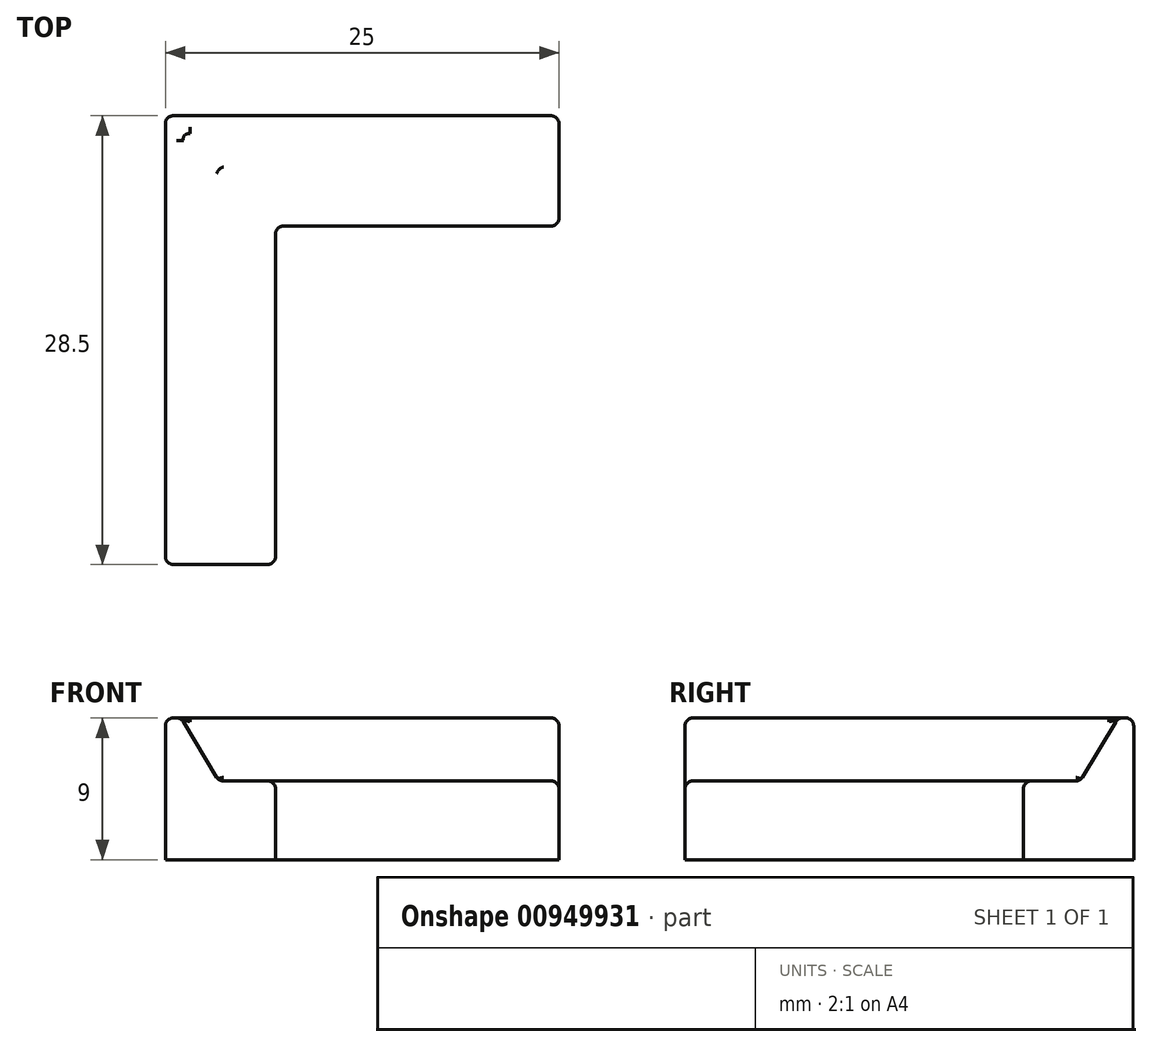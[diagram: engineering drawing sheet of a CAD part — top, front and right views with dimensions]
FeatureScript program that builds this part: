
annotation { "Feature Type Name" : "Feature", "Feature Type Description" : "" }
export const myFeature = defineFeature(function(context is Context, id is Id, definition is map)
    precondition{}
    {
        {
            var Q0;
            Q0=qCreatedBy(makeId("Top.planeOp"),FACE);
            var sketch = newSketch(context, id + "F0", { "sketchPlane" : qUnion([Q0])});
            skLineSegment(sketch, "E0.bottom", {"start": v(-48.09, 20.85) * mm, "end": v(-41.09, 20.85) * mm});
            skLineSegment(sketch, "E0.top", {"start": v(-48.09, -7.65) * mm, "end": v(-41.09, -7.65) * mm});
            skLineSegment(sketch, "E0.left", {"start": v(-48.09, 20.85) * mm, "end": v(-48.09, -7.65) * mm});
            skLineSegment(sketch, "E0.right", {"start": v(-41.09, 20.85) * mm, "end": v(-41.09, -7.65) * mm});
            skLineSegment(sketch, "E1.bottom", {"start": v(-41.09, 20.85) * mm, "end": v(-23.09, 20.85) * mm});
            skLineSegment(sketch, "E1.top", {"start": v(-41.09, 13.85) * mm, "end": v(-23.09, 13.85) * mm});
            skLineSegment(sketch, "E1.left", {"start": v(-41.09, 20.85) * mm, "end": v(-41.09, 13.85) * mm});
            skLineSegment(sketch, "E1.right", {"start": v(-23.09, 20.85) * mm, "end": v(-23.09, 13.85) * mm});
            skSolve(sketch);
        }
        {
            var Q0;
            Q0 = qSketchRegion(id + "F0", true);
            extrude(context, id + "F1", {"entities" : qUnion([Q0]), "depth" : 5 * mm, "offsetDistance" : 25 * mm});
        }
        {
            var Q0;
            Q0=makeQuery(id+"F1.opExtrude","CAP_FACE",FACE,{"disambiguationData":[OSD([sQuery(id+"F0.wireOp",EDGE,"E0.bottom"),sQuery(id+"F0.wireOp",EDGE,"E0.top"),sQuery(id+"F0.wireOp",EDGE,"E0.left"),sQuery(id+"F0.wireOp",EDGE,"E0.right"),sQuery(id+"F0.wireOp",EDGE,"E1.bottom"),sQuery(id+"F0.wireOp",EDGE,"E1.top"),sQuery(id+"F0.wireOp",EDGE,"E1.right")])],"isStart":false});
            var sketch = newSketch(context, id + "F2", { "sketchPlane" : qUnion([Q0])});
            skLineSegment(sketch, "E2.bottom", {"start": v(-48.09, 20.85) * mm, "end": v(-44.09, 20.85) * mm});
            skLineSegment(sketch, "E2.top", {"start": v(-48.09, -7.65) * mm, "end": v(-44.09, -7.65) * mm});
            skLineSegment(sketch, "E2.left", {"start": v(-48.09, 20.85) * mm, "end": v(-48.09, -7.65) * mm});
            skLineSegment(sketch, "E2.right", {"start": v(-44.09, 20.85) * mm, "end": v(-44.09, -7.65) * mm});
            skLineSegment(sketch, "E3.bottom", {"start": v(-44.09, 20.85) * mm, "end": v(-23.09, 20.85) * mm});
            skLineSegment(sketch, "E3.top", {"start": v(-44.09, 16.85) * mm, "end": v(-23.09, 16.85) * mm});
            skLineSegment(sketch, "E3.left", {"start": v(-44.09, 20.85) * mm, "end": v(-44.09, 16.85) * mm});
            skLineSegment(sketch, "E3.right", {"start": v(-23.09, 20.85) * mm, "end": v(-23.09, 16.85) * mm});
            skSolve(sketch);
        }
        {
            var Q0;
            Q0 = qSketchRegion(id + "F2", true);
            extrude(context, id + "F3", {"entities" : qUnion([Q0]), "operationType" : NewBodyOperationType.ADD, "depth" : 4 * mm, "offsetDistance" : 25 * mm});
        }
        {
            var Q0;
            Q0=makeQuery(id+"F3.opExtrude","CAP_EDGE",EDGE,{"disambiguationData":[OSD([sQuery(id+"F2.wireOp",EDGE,"E2.right")])],"isStart":false});
            var Q1;
            Q1=makeQuery(id+"F3.opExtrude","CAP_EDGE",EDGE,{"disambiguationData":[OSD([sQuery(id+"F2.wireOp",EDGE,"E3.top")])],"isStart":false});
            chamfer(context, id + "F4", {"entities" : qUnion([Q0, Q1]), "chamferType" : ChamferType.TWO_OFFSETS, "width1" : 5 * mm, "oppositeDirection" : false, "width2" : 3 * mm, "tangentPropagation" : true});
        }
        {
            var Q0;
            Q0=makeQuery(id+"F3.boolean.opBoolean","MERGE",EDGE,{"derivedFrom":[makeQuery(id+"F1.opExtrude","SWEPT_EDGE",EDGE,{"disambiguationData":[OSD([sQuery(id+"F0.wireOp",EDGE,"E0.top"),sQuery(id+"F0.wireOp",EDGE,"E0.left")])]}),makeQuery(id+"F3.opExtrude","SWEPT_EDGE",EDGE,{"disambiguationData":[OSD([sQuery(id+"F2.wireOp",EDGE,"E2.top"),sQuery(id+"F2.wireOp",EDGE,"E2.left")])]})]});
            var Q1;
            Q1=makeQuery(id+"F1.opExtrude","SWEPT_EDGE",EDGE,{"disambiguationData":[OSD([sQuery(id+"F0.wireOp",EDGE,"E0.top"),sQuery(id+"F0.wireOp",EDGE,"E0.right")])]});
            var Q2;
            Q2=makeQuery(id+"F1.opExtrude","SWEPT_EDGE",EDGE,{"disambiguationData":[OSD([sQuery(id+"F0.wireOp",EDGE,"E0.right"),sQuery(id+"F0.wireOp",EDGE,"E1.top"),sQuery(id+"F0.wireOp",EDGE,"E1.left")])]});
            var Q3;
            Q3=makeQuery(id+"F1.opExtrude","SWEPT_EDGE",EDGE,{"disambiguationData":[OSD([sQuery(id+"F0.wireOp",EDGE,"E1.top"),sQuery(id+"F0.wireOp",EDGE,"E1.right")])]});
            var Q4;
            Q4=makeQuery(id+"F3.boolean.opBoolean","MERGE",EDGE,{"derivedFrom":[makeQuery(id+"F1.opExtrude","SWEPT_EDGE",EDGE,{"disambiguationData":[OSD([sQuery(id+"F0.wireOp",EDGE,"E1.bottom"),sQuery(id+"F0.wireOp",EDGE,"E1.right")])]}),makeQuery(id+"F3.opExtrude","SWEPT_EDGE",EDGE,{"disambiguationData":[OSD([sQuery(id+"F2.wireOp",EDGE,"E3.bottom"),sQuery(id+"F2.wireOp",EDGE,"E3.right")])]})]});
            var Q5;
            Q5=makeQuery(id+"F3.opExtrude","CAP_EDGE",EDGE,{"disambiguationData":[OSD([sQuery(id+"F2.wireOp",EDGE,"E2.bottom"),sQuery(id+"F2.wireOp",EDGE,"E3.bottom")])],"isStart":false});
            var Q6;
            {var subQ0=sQuery(id+"F2.wireOp",EDGE,"E3.top");Q6=makeQuery(id+"F4.opChamfer","BLEND_EDGE",EDGE,{"blendedFrom":[makeQuery(id+"F3.opExtrude","CAP_EDGE",EDGE,{"disambiguationData":[OSD([subQ0])],"isStart":false}),makeQuery(id+"F3.opExtrude","CAP_FACE",FACE,{"disambiguationData":[OSD([sQuery(id+"F2.wireOp",EDGE,"E2.bottom"),sQuery(id+"F2.wireOp",EDGE,"E2.top"),sQuery(id+"F2.wireOp",EDGE,"E2.left"),sQuery(id+"F2.wireOp",EDGE,"E2.right"),sQuery(id+"F2.wireOp",EDGE,"E3.bottom"),subQ0,sQuery(id+"F2.wireOp",EDGE,"E3.right")])],"isStart":false})],"blendedInto":[makeQuery(id+"F3.opExtrude","CAP_FACE",FACE,{"disambiguationData":[OSD([sQuery(id+"F2.wireOp",EDGE,"E2.bottom"),sQuery(id+"F2.wireOp",EDGE,"E2.top"),sQuery(id+"F2.wireOp",EDGE,"E2.left"),sQuery(id+"F2.wireOp",EDGE,"E2.right"),sQuery(id+"F2.wireOp",EDGE,"E3.bottom"),subQ0,sQuery(id+"F2.wireOp",EDGE,"E3.right")])],"isStart":false})]});}
            var Q7;
            {var subQ0=sQuery(id+"F2.wireOp",EDGE,"E2.right");Q7=makeQuery(id+"F4.opChamfer","BLEND_EDGE",EDGE,{"blendedFrom":[makeQuery(id+"F3.opExtrude","CAP_EDGE",EDGE,{"disambiguationData":[OSD([subQ0])],"isStart":false}),makeQuery(id+"F3.opExtrude","CAP_FACE",FACE,{"disambiguationData":[OSD([sQuery(id+"F2.wireOp",EDGE,"E2.bottom"),sQuery(id+"F2.wireOp",EDGE,"E2.top"),sQuery(id+"F2.wireOp",EDGE,"E2.left"),subQ0,sQuery(id+"F2.wireOp",EDGE,"E3.bottom"),sQuery(id+"F2.wireOp",EDGE,"E3.top"),sQuery(id+"F2.wireOp",EDGE,"E3.right")])],"isStart":false})],"blendedInto":[makeQuery(id+"F3.opExtrude","CAP_FACE",FACE,{"disambiguationData":[OSD([sQuery(id+"F2.wireOp",EDGE,"E2.bottom"),sQuery(id+"F2.wireOp",EDGE,"E2.top"),sQuery(id+"F2.wireOp",EDGE,"E2.left"),subQ0,sQuery(id+"F2.wireOp",EDGE,"E3.bottom"),sQuery(id+"F2.wireOp",EDGE,"E3.top"),sQuery(id+"F2.wireOp",EDGE,"E3.right")])],"isStart":false})]});}
            var Q8;
            Q8=makeQuery(id+"F4.opChamfer","BLEND_EDGE",EDGE,{"blendedFrom":[makeQuery(id+"F3.opExtrude","CAP_EDGE",EDGE,{"disambiguationData":[OSD([sQuery(id+"F2.wireOp",EDGE,"E2.right")])],"isStart":false}),makeQuery(id+"F3.opExtrude","CAP_EDGE",EDGE,{"disambiguationData":[OSD([sQuery(id+"F2.wireOp",EDGE,"E3.top")])],"isStart":false})],"blendedInto":[]});
            var Q9;
            Q9=makeQuery(id+"F4.opChamfer","BLEND_EDGE",EDGE,{"blendedFrom":[makeQuery(id+"F3.opExtrude","CAP_EDGE",EDGE,{"disambiguationData":[OSD([sQuery(id+"F2.wireOp",EDGE,"E3.top")])],"isStart":false}),makeQuery(id+"F1.opExtrude","CAP_FACE",FACE,{"disambiguationData":[OSD([sQuery(id+"F0.wireOp",EDGE,"E0.bottom"),sQuery(id+"F0.wireOp",EDGE,"E0.top"),sQuery(id+"F0.wireOp",EDGE,"E0.left"),sQuery(id+"F0.wireOp",EDGE,"E0.right"),sQuery(id+"F0.wireOp",EDGE,"E1.bottom"),sQuery(id+"F0.wireOp",EDGE,"E1.top"),sQuery(id+"F0.wireOp",EDGE,"E1.right")])],"isStart":false})],"blendedInto":[makeQuery(id+"F1.opExtrude","CAP_FACE",FACE,{"disambiguationData":[OSD([sQuery(id+"F0.wireOp",EDGE,"E0.bottom"),sQuery(id+"F0.wireOp",EDGE,"E0.top"),sQuery(id+"F0.wireOp",EDGE,"E0.left"),sQuery(id+"F0.wireOp",EDGE,"E0.right"),sQuery(id+"F0.wireOp",EDGE,"E1.bottom"),sQuery(id+"F0.wireOp",EDGE,"E1.top"),sQuery(id+"F0.wireOp",EDGE,"E1.right")])],"isStart":false})]});
            var Q10;
            Q10=makeQuery(id+"F4.opChamfer","BLEND_EDGE",EDGE,{"blendedFrom":[makeQuery(id+"F3.opExtrude","CAP_EDGE",EDGE,{"disambiguationData":[OSD([sQuery(id+"F2.wireOp",EDGE,"E2.right")])],"isStart":false}),makeQuery(id+"F1.opExtrude","CAP_FACE",FACE,{"disambiguationData":[OSD([sQuery(id+"F0.wireOp",EDGE,"E0.bottom"),sQuery(id+"F0.wireOp",EDGE,"E0.top"),sQuery(id+"F0.wireOp",EDGE,"E0.left"),sQuery(id+"F0.wireOp",EDGE,"E0.right"),sQuery(id+"F0.wireOp",EDGE,"E1.bottom"),sQuery(id+"F0.wireOp",EDGE,"E1.top"),sQuery(id+"F0.wireOp",EDGE,"E1.right")])],"isStart":false})],"blendedInto":[makeQuery(id+"F1.opExtrude","CAP_FACE",FACE,{"disambiguationData":[OSD([sQuery(id+"F0.wireOp",EDGE,"E0.bottom"),sQuery(id+"F0.wireOp",EDGE,"E0.top"),sQuery(id+"F0.wireOp",EDGE,"E0.left"),sQuery(id+"F0.wireOp",EDGE,"E0.right"),sQuery(id+"F0.wireOp",EDGE,"E1.bottom"),sQuery(id+"F0.wireOp",EDGE,"E1.top"),sQuery(id+"F0.wireOp",EDGE,"E1.right")])],"isStart":false})]});
            var Q11;
            Q11=makeQuery(id+"F1.opExtrude","CAP_EDGE",EDGE,{"disambiguationData":[OSD([sQuery(id+"F0.wireOp",EDGE,"E0.right")])],"isStart":false});
            var Q12;
            Q12=makeQuery(id+"F1.opExtrude","CAP_EDGE",EDGE,{"disambiguationData":[OSD([sQuery(id+"F0.wireOp",EDGE,"E1.top")])],"isStart":false});
            var Q13;
            Q13=makeQuery(id+"F3.opExtrude","CAP_EDGE",EDGE,{"disambiguationData":[OSD([sQuery(id+"F2.wireOp",EDGE,"E2.left")])],"isStart":false});
            var Q14;
            Q14=makeQuery(id+"F3.boolean.opBoolean","MERGE",EDGE,{"derivedFrom":[makeQuery(id+"F1.opExtrude","SWEPT_EDGE",EDGE,{"disambiguationData":[OSD([sQuery(id+"F0.wireOp",EDGE,"E0.bottom"),sQuery(id+"F0.wireOp",EDGE,"E0.left")])]}),makeQuery(id+"F3.opExtrude","SWEPT_EDGE",EDGE,{"disambiguationData":[OSD([sQuery(id+"F2.wireOp",EDGE,"E2.bottom"),sQuery(id+"F2.wireOp",EDGE,"E2.left")])]})]});
            fillet(context, id + "F5", {"entities" : qUnion([Q0, Q1, Q2, Q3, Q4, Q5, Q6, Q7, Q8, Q9, Q10, Q11, Q12, Q13, Q14]), "radius" : 0.5 * mm, "tangentPropagation" : true, "allowEdgeOverflow" : false});
        }
        {
            var Q0;
            Q0=makeQuery(id+"F1.opExtrude","CAP_EDGE",EDGE,{"disambiguationData":[OSD([sQuery(id+"F0.wireOp",EDGE,"E0.top")])],"isStart":false});
            var Q1;
            Q1=makeQuery(id+"F1.opExtrude","CAP_EDGE",EDGE,{"disambiguationData":[OSD([sQuery(id+"F0.wireOp",EDGE,"E1.right")])],"isStart":false});
            fillet(context, id + "F6", {"entities" : qUnion([Q0, Q1]), "radius" : 0.5 * mm, "tangentPropagation" : true, "allowEdgeOverflow" : false});
        }
    });
